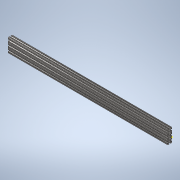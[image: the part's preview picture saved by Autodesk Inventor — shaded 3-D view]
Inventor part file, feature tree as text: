
AUTODESK INVENTOR PART (.ipt)
format: ipt  version: 2020 (Build 240168000, 168)  size: 396,800 bytes
history: native  units: in
note: dims shown in document units (in); Inventor stores cm internally (conversion verified against a paired STEP export)
features: sketch x2, extrude x1
ambient origin geometry x8: Origin, YZ Plane, XZ Plane, XY Plane, X Axis, Y Axis, Z Axis, Center Point
bodies: Solid1 (feature_tree)
feature tree (3):
  extrude  "Extrusion1"  [1 undecoded]
  sketch  "Sketch2"
  sketch  "Sketch1"  dims[d0=35.0in d1=0.0in]
note: 1 required parameter value undecoded (feature->parameter linkage not recoverable at this tier; creation-order binding heuristic only, values carry confidence <= 0.55)
